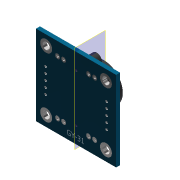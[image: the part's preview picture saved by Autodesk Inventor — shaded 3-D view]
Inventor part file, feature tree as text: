
AUTODESK INVENTOR PART (.ipt)
format: ipt  version: 2016 (Build 200138000, 138)  size: 1,490,944 bytes
history: native  units: mm
features: sketch x20, extrude x14, projected_geometry x8, hole x4, mirror x4, fillet x2, thread x1, plane x1
ambient origin geometry x8: Origin, YZ Plane, XZ Plane, XY Plane, X Axis, Y Axis, Z Axis, Center Point
bodies: Solid1 (feature_tree)
feature tree (54):
  extrude  "Extrusion1"  Depth=33.5mm
  hole  "Hole1"  [1 undecoded]
  extrude  "Extrusion2"  Depth=25.0mm
  extrude  "Extrusion3"  TaperAngle=0.0deg  [1 undecoded]
  hole  "Hole2"  [1 undecoded]
  mirror  "Mirror1"
  extrude  "Extrusion4"  Depth=5.0mm
  mirror  "Mirror2"
  extrude  "Extrusion5"  Depth=5.0mm
  mirror  "Mirror3"
  extrude  "Extrusion6"  Depth=0.01mm TaperAngle=0.0deg
  extrude  "Extrusion7"  Depth=4.0mm
  hole  "Hole3"  [1 undecoded]
  extrude  "Extrusion8"  Depth=2.0mm
  extrude  "Extrusion9"  Depth=2.0mm
  mirror  "Mirror4"
  extrude  "Extrusion10"  Depth=0.01mm TaperAngle=0.0deg
  extrude  "Extrusion11"  Depth=13.0mm
  hole  "Hole4"  [1 undecoded]
  extrude  "Extrusion12"  Depth=0.01mm TaperAngle=0.0deg
  fillet  "Fillet1"  Radius=0.01mm
  fillet  "Fillet2"  Radius=2.54mm
  extrude  "Extrusion13"  Depth=9.0mm
  extrude  "Extrusion14"  Depth=5.5mm
  sketch  "Sketch19"  dims[d62=2.54mm d63=5.5mm d64=9.0mm]
  sketch  "Sketch20"  dims[d65=1.0mm d66=6.0mm d67=4.0mm d68=2.0mm d69=90.0deg d70=8.0mm d71=20.594885mm d72=2.0mm d73=2.0mm d74=2.0mm d75=2.0mm d76=0.01mm d77=0.0mm d78=2.0mm d79=2.0mm d80=2.0mm d81=2.0mm d82=0.01mm d83=0.0mm d84=16.0mm d85=16.0mm d86=10.0mm d87=4.3mm d88=7.0mm d89=0.0mm d90=15.8mm d91=3.0mm d92=0.0mm d93=1.0mm d94=6.0mm d95=4.0mm d96=2.0mm d97=90.0deg d98=8.0mm d99=20.594885mm d100=3.5mm d101=0.9mm d102=1.5mm d103=0.0mm d104=0.0mm d105=0.02mm d106=0.02mm d107=2.14mm d108=0.9mm d109=0.0mm d111=1.0mm d112=1.0mm d113=6.4mm d114=0.0mm d115=10.0mm d116=0.0mm]
  thread  "Thread1"  [1 undecoded]
  sketch  "Sketch1"  dims[d0=33.5mm d1=33.5mm]
  sketch  "Sketch2"  dims[d2=1.65mm d3=0.0mm d4=25.0mm]
  sketch  "Sketch3"  dims[d5=25.0mm d6=25.0mm]
  projected_geometry  "Projected Loop1"
  sketch  "Sketch4"  dims[d7=25.0mm d8=0.0mm]
  projected_geometry  "Projected Loop2"
  sketch  "Sketch5"  dims[d9=4.25mm d10=4.25mm]
  plane  "Work Plane1"
  sketch  "Sketch6"  dims[d11=3.0mm d12=6.0mm d13=4.0mm d14=2.0mm d15=90.0deg d16=8.0mm d17=20.594885mm d18=5.0mm]
  projected_geometry  "Projected Loop3"
  sketch  "Sketch7"  dims[d19=5.0mm d20=5.0mm]
  sketch  "Sketch8"  dims[d21=5.0mm d22=0.01mm d23=0.0mm]
  sketch  "Sketch9"  dims[d24=0.01mm d25=0.0mm d26=4.0mm]
  sketch  "Sketch10"  dims[d27=50.0mm d29=2.54mm d30=10.0mm d32=10.0mm]
  sketch  "Sketch11"  dims[d34=1.0mm d35=6.0mm d36=4.0mm d37=2.0mm d38=90.0deg d39=8.0mm d40=20.594885mm d41=11.68mm]
  projected_geometry  "Projected Loop4"
  sketch  "Sketch12"  dims[d42=2.0mm d43=2.0mm]
  projected_geometry  "Projected Loop5"
  sketch  "Sketch13"  dims[d44=2.0mm d45=2.0mm]
  sketch  "Sketch14"  dims[d46=2.0mm d47=0.01mm d48=0.0mm]
  sketch  "Sketch15"  dims[d49=3.3mm d50=13.0mm]
  projected_geometry  "Projected Loop6"
  sketch  "Sketch16"  dims[d51=0.4mm d52=0.4mm]
  sketch  "Sketch17"  dims[d53=0.01mm d54=0.0mm d55=0.01mm d56=0.0mm d57=0.01mm d58=0.0mm d59=2.54mm]
  sketch  "Sketch18"  dims[d60=5.5mm d61=9.0mm]
  projected_geometry  "Projected Loop7"
  projected_geometry  "Projected Loop8"
note: 6 required parameter values undecoded (feature->parameter linkage not recoverable at this tier; creation-order binding heuristic only, values carry confidence <= 0.55)
